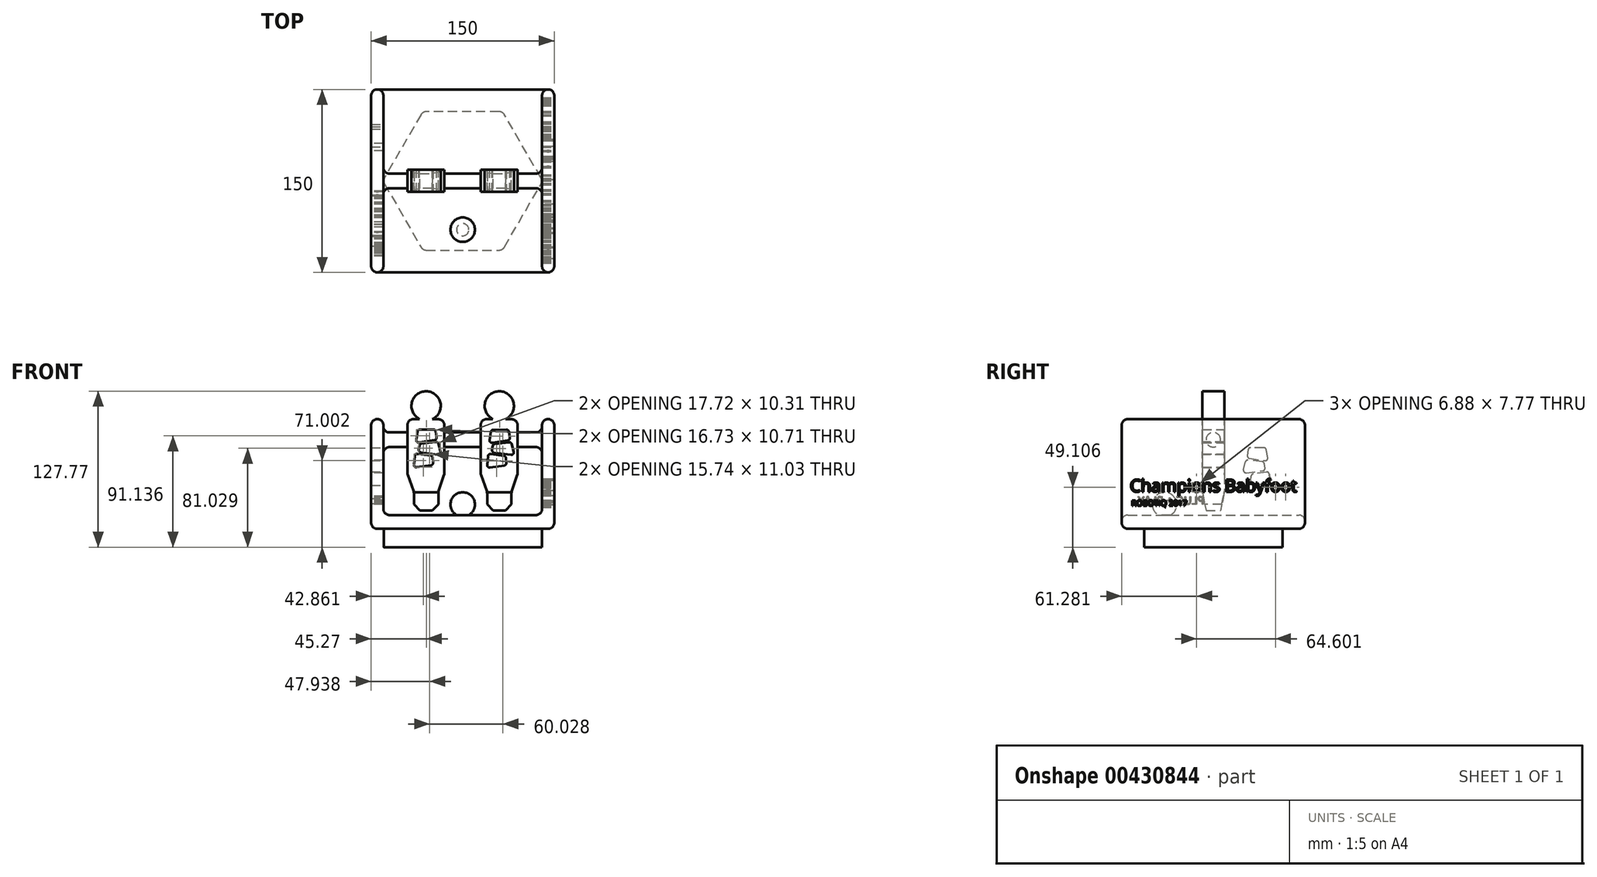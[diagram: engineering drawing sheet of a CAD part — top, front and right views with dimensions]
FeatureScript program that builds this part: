
annotation { "Feature Type Name" : "Feature", "Feature Type Description" : "" }
export const myFeature = defineFeature(function(context is Context, id is Id, definition is map)
    precondition{}
    {
        {
            var Q0;
            Q0=qCreatedBy(makeId("Front.planeOp"),FACE);
            var sketch = newSketch(context, id + "F0", { "sketchPlane" : qUnion([Q0])});
            skLineSegment(sketch, "E0.left", {"start": v(-40, 15) * mm, "end": v(-40, 0) * mm});
            skLineSegment(sketch, "E0.right", {"start": v(-20, 15) * mm, "end": v(-20, 0) * mm});
            skLineSegment(sketch, "E1", {"start": v(-45.3, 75) * mm, "end": v(-35.3, 75) * mm});
            skLineSegment(sketch, "E2", {"start": v(-25, 74.86) * mm, "end": v(-15, 74.86) * mm});
            skArc(sketch, "E3", {"start": v(-25, 74.86) * mm, "mid": v(-29.84, 97.77) * mm, "end": v(-35.3, 75) * mm});
            skLineSegment(sketch, "E4", {"start": v(-40, 0) * mm, "end": v(-30, 0) * mm});
            skLineSegment(sketch, "E5", {"start": v(-30, 0) * mm, "end": v(-20, 0) * mm});
            skLineSegment(sketch, "E6", {"start": v(-15, 74.86) * mm, "end": v(-15, 29.86) * mm});
            skLineSegment(sketch, "E7", {"start": v(-15, 29.86) * mm, "end": v(-20, 15) * mm});
            skLineSegment(sketch, "E8", {"start": v(-45.3, 75) * mm, "end": v(-45.3, 30) * mm});
            skLineSegment(sketch, "E9", {"start": v(-45.3, 30) * mm, "end": v(-40, 15) * mm});
            skLineSegment(sketch, "E10.left", {"start": v(20, 15) * mm, "end": v(20, 0) * mm});
            skLineSegment(sketch, "E10.right", {"start": v(40, 15) * mm, "end": v(40, 0) * mm});
            skLineSegment(sketch, "E11", {"start": v(14.7, 75) * mm, "end": v(24.7, 75) * mm});
            skLineSegment(sketch, "E12", {"start": v(35, 74.86) * mm, "end": v(45, 74.86) * mm});
            skArc(sketch, "E13", {"start": v(35, 74.86) * mm, "mid": v(30.16, 97.77) * mm, "end": v(24.7, 75) * mm});
            skLineSegment(sketch, "E14", {"start": v(20, 0) * mm, "end": v(30, 0) * mm});
            skLineSegment(sketch, "E15", {"start": v(30, 0) * mm, "end": v(40, 0) * mm});
            skLineSegment(sketch, "E16", {"start": v(45, 74.86) * mm, "end": v(45, 29.86) * mm});
            skLineSegment(sketch, "E17", {"start": v(45, 29.86) * mm, "end": v(40, 15) * mm});
            skLineSegment(sketch, "E18", {"start": v(14.7, 75) * mm, "end": v(14.7, 30) * mm});
            skLineSegment(sketch, "E19", {"start": v(14.7, 30) * mm, "end": v(20, 15) * mm});
            skSolve(sketch);
        }
        {
            var Q0;
            Q0 = qSketchRegion(id + "F0", true);
            extrude(context, id + "F1", {"entities" : qUnion([Q0]), "endBound" : BoundingType.SYMMETRIC, "depth" : 18 * mm});
        }
        {
            var Q0;
            Q0=makeQuery(id+"F1.opExtrude","SWEPT_EDGE",EDGE,{"disambiguationData":[OSD([sQuery(id+"F0.wireOp",EDGE,"E1"),sQuery(id+"F0.wireOp",EDGE,"E8")])]});
            var Q1;
            Q1=makeQuery(id+"F1.opExtrude","SWEPT_EDGE",EDGE,{"disambiguationData":[OSD([sQuery(id+"F0.wireOp",EDGE,"E8"),sQuery(id+"F0.wireOp",EDGE,"E9")])]});
            var Q2;
            Q2=makeQuery(id+"F1.opExtrude","SWEPT_EDGE",EDGE,{"disambiguationData":[OSD([sQuery(id+"F0.wireOp",EDGE,"E0.left"),sQuery(id+"F0.wireOp",EDGE,"E9")])]});
            var Q3;
            Q3=makeQuery(id+"F1.opExtrude","SWEPT_EDGE",EDGE,{"disambiguationData":[OSD([sQuery(id+"F0.wireOp",EDGE,"E10.left"),sQuery(id+"F0.wireOp",EDGE,"E19")])]});
            var Q4;
            Q4=makeQuery(id+"F1.opExtrude","SWEPT_EDGE",EDGE,{"disambiguationData":[OSD([sQuery(id+"F0.wireOp",EDGE,"E18"),sQuery(id+"F0.wireOp",EDGE,"E19")])]});
            var Q5;
            Q5=makeQuery(id+"F1.opExtrude","SWEPT_EDGE",EDGE,{"disambiguationData":[OSD([sQuery(id+"F0.wireOp",EDGE,"E11"),sQuery(id+"F0.wireOp",EDGE,"E18")])]});
            var Q6;
            Q6=makeQuery(id+"F1.opExtrude","SWEPT_EDGE",EDGE,{"disambiguationData":[OSD([sQuery(id+"F0.wireOp",EDGE,"E2"),sQuery(id+"F0.wireOp",EDGE,"E6")])]});
            var Q7;
            Q7=makeQuery(id+"F1.opExtrude","SWEPT_EDGE",EDGE,{"disambiguationData":[OSD([sQuery(id+"F0.wireOp",EDGE,"E6"),sQuery(id+"F0.wireOp",EDGE,"E7")])]});
            var Q8;
            Q8=makeQuery(id+"F1.opExtrude","SWEPT_EDGE",EDGE,{"disambiguationData":[OSD([sQuery(id+"F0.wireOp",EDGE,"E0.right"),sQuery(id+"F0.wireOp",EDGE,"E7")])]});
            var Q9;
            Q9=makeQuery(id+"F1.opExtrude","SWEPT_EDGE",EDGE,{"disambiguationData":[OSD([sQuery(id+"F0.wireOp",EDGE,"E10.right"),sQuery(id+"F0.wireOp",EDGE,"E17")])]});
            var Q10;
            Q10=makeQuery(id+"F1.opExtrude","SWEPT_EDGE",EDGE,{"disambiguationData":[OSD([sQuery(id+"F0.wireOp",EDGE,"E16"),sQuery(id+"F0.wireOp",EDGE,"E17")])]});
            var Q11;
            Q11=makeQuery(id+"F1.opExtrude","SWEPT_EDGE",EDGE,{"disambiguationData":[OSD([sQuery(id+"F0.wireOp",EDGE,"E12"),sQuery(id+"F0.wireOp",EDGE,"E16")])]});
            fillet(context, id + "F2", {"entities" : qUnion([Q0, Q1, Q2, Q3, Q4, Q5, Q6, Q7, Q8, Q9, Q10, Q11]), "radius" : 5 * mm, "tangentPropagation" : true, "allowEdgeOverflow" : false});
        }
        {
            var Q0;
            Q0=makeQuery(id+"F1.opExtrude","SWEPT_EDGE",EDGE,{"disambiguationData":[OSD([sQuery(id+"F0.wireOp",EDGE,"E0.left"),sQuery(id+"F0.wireOp",EDGE,"E4")])]});
            var Q1;
            Q1=makeQuery(id+"F1.opExtrude","SWEPT_EDGE",EDGE,{"disambiguationData":[OSD([sQuery(id+"F0.wireOp",EDGE,"E0.right"),sQuery(id+"F0.wireOp",EDGE,"E5")])]});
            var Q2;
            Q2=makeQuery(id+"F1.opExtrude","SWEPT_EDGE",EDGE,{"disambiguationData":[OSD([sQuery(id+"F0.wireOp",EDGE,"E10.right"),sQuery(id+"F0.wireOp",EDGE,"E15")])]});
            var Q3;
            Q3=makeQuery(id+"F1.opExtrude","SWEPT_EDGE",EDGE,{"disambiguationData":[OSD([sQuery(id+"F0.wireOp",EDGE,"E10.left"),sQuery(id+"F0.wireOp",EDGE,"E14")])]});
            chamfer(context, id + "F3", {"entities" : qUnion([Q0, Q1, Q2, Q3]), "width" : 5 * mm, "tangentPropagation" : true});
        }
        {
            var Q0;
            Q0=makeQuery(id+"F1.opExtrude","CAP_EDGE",EDGE,{"disambiguationData":[OSD([sQuery(id+"F0.wireOp",EDGE,"E4"),sQuery(id+"F0.wireOp",EDGE,"E5")])],"isStart":false});
            var Q1;
            Q1=makeQuery(id+"F1.opExtrude","CAP_EDGE",EDGE,{"disambiguationData":[OSD([sQuery(id+"F0.wireOp",EDGE,"E14"),sQuery(id+"F0.wireOp",EDGE,"E15")])],"isStart":false});
            var Q2;
            Q2=makeQuery(id+"F1.opExtrude","CAP_EDGE",EDGE,{"disambiguationData":[OSD([sQuery(id+"F0.wireOp",EDGE,"E14"),sQuery(id+"F0.wireOp",EDGE,"E15")])],"isStart":true});
            var Q3;
            Q3=makeQuery(id+"F1.opExtrude","CAP_EDGE",EDGE,{"disambiguationData":[OSD([sQuery(id+"F0.wireOp",EDGE,"E4"),sQuery(id+"F0.wireOp",EDGE,"E5")])],"isStart":true});
            chamfer(context, id + "F4", {"entities" : qUnion([Q0, Q1, Q2, Q3]), "chamferType" : ChamferType.TWO_OFFSETS, "width1" : 15 * mm, "oppositeDirection" : false, "width2" : 3 * mm, "tangentPropagation" : true});
        }
        {
            var Q0;
            Q0=qCreatedBy(makeId("Right.planeOp"),FACE);
            var sketch = newSketch(context, id + "F5", { "sketchPlane" : qUnion([Q0])});
            skCircle(sketch, "E20", {"center": v(0, 58) * mm, "radius": 6 * mm});
            skSolve(sketch);
        }
        {
            var Q0;
            Q0 = qSketchRegion(id + "F5", true);
            extrude(context, id + "F6", {"entities" : qUnion([Q0]), "operationType" : NewBodyOperationType.ADD, "endBound" : BoundingType.SYMMETRIC, "depth" : 150 * mm});
        }
        {
            var Q0;
            Q0=qCreatedBy(makeId("Front.planeOp"),FACE);
            cPlane(context, id + "F7", {"entities" : qUnion([Q0]), "cplaneType" : CPlaneType.OFFSET, "offset" : 40 * mm, "width" : 150 * mm, "height" : 150 * mm});
        }
        {
            var Q0;
            Q0=qCreatedBy(id+"F7.planeOp",FACE);
            var sketch = newSketch(context, id + "F8", { "sketchPlane" : qUnion([Q0])});
            skPoint(sketch, "E21", {"position": v(0, 4.98) * mm});
            skLineSegment(sketch, "E22", {"start": v(-10, 4.93) * mm, "end": v(10, 4.93) * mm});
            skArc(sketch, "E23", {"start": v(10, 4.93) * mm, "mid": v(0, 14.93) * mm, "end": v(-10, 4.93) * mm});
            skSolve(sketch);
        }
        {
            var Q0;
            Q0=qCreatedBy(makeId("Front.planeOp"),FACE);
            var sketch = newSketch(context, id + "F9", { "sketchPlane" : qUnion([Q0])});
            skLineSegment(sketch, "E24.top", {"start": v(-75, -15) * mm, "end": v(75, -15) * mm});
            skLineSegment(sketch, "E25", {"start": v(75, -15) * mm, "end": v(75, 75) * mm});
            skLineSegment(sketch, "E26", {"start": v(75, 75) * mm, "end": v(65, 75) * mm});
            skLineSegment(sketch, "E27", {"start": v(65, 75) * mm, "end": v(65, 0) * mm});
            skLineSegment(sketch, "E28", {"start": v(-65, 1.11) * mm, "end": v(-65, 75) * mm});
            skLineSegment(sketch, "E29", {"start": v(-75, -15) * mm, "end": v(-75, 75) * mm});
            skLineSegment(sketch, "E30", {"start": v(-75, 75) * mm, "end": v(-65, 75) * mm});
            skLineSegment(sketch, "E31", {"start": v(65, 0) * mm, "end": v(65, -3.72) * mm});
            skLineSegment(sketch, "E32", {"start": v(65, -3.72) * mm, "end": v(-65, -3.72) * mm});
            skLineSegment(sketch, "E33", {"start": v(-65, 1.11) * mm, "end": v(-65, -3.72) * mm});
            skSolve(sketch);
        }
        {
            var Q0;
            Q0 = qSketchRegion(id + "F9", true);
            extrude(context, id + "F10", {"entities" : qUnion([Q0]), "operationType" : NewBodyOperationType.ADD, "endBound" : BoundingType.SYMMETRIC, "depth" : 150 * mm});
        }
        {
            var Q0;
            Q0=makeQuery(id+"F10.opExtrude","SWEPT_EDGE",EDGE,{"disambiguationData":[OSD([sQuery(id+"F9.wireOp",EDGE,"E29"),sQuery(id+"F9.wireOp",EDGE,"E30")])]});
            var Q1;
            Q1=makeQuery(id+"F10.opExtrude","CAP_EDGE",EDGE,{"disambiguationData":[OSD([sQuery(id+"F9.wireOp",EDGE,"E30")])],"isStart":false});
            var Q2;
            Q2=makeQuery(id+"F10.opExtrude","CAP_EDGE",EDGE,{"disambiguationData":[OSD([sQuery(id+"F9.wireOp",EDGE,"E30")])],"isStart":true});
            var Q3;
            Q3=makeQuery(id+"F10.opExtrude","SWEPT_EDGE",EDGE,{"disambiguationData":[OSD([sQuery(id+"F9.wireOp",EDGE,"E28"),sQuery(id+"F9.wireOp",EDGE,"E30")])]});
            var Q4;
            Q4=makeQuery(id+"F10.opExtrude","CAP_EDGE",EDGE,{"disambiguationData":[OSD([sQuery(id+"F9.wireOp",EDGE,"E28"),sQuery(id+"F9.wireOp",EDGE,"E33")])],"isStart":true});
            var Q5;
            Q5=makeQuery(id+"F10.opExtrude","CAP_EDGE",EDGE,{"disambiguationData":[OSD([sQuery(id+"F9.wireOp",EDGE,"E29")])],"isStart":true});
            var Q6;
            Q6=makeQuery(id+"F10.opExtrude","CAP_EDGE",EDGE,{"disambiguationData":[OSD([sQuery(id+"F9.wireOp",EDGE,"E29")])],"isStart":false});
            var Q7;
            Q7=makeQuery(id+"F10.opExtrude","CAP_EDGE",EDGE,{"disambiguationData":[OSD([sQuery(id+"F9.wireOp",EDGE,"E28"),sQuery(id+"F9.wireOp",EDGE,"E33")])],"isStart":false});
            var Q8;
            Q8=makeQuery(id+"F10.opExtrude","CAP_EDGE",EDGE,{"disambiguationData":[OSD([sQuery(id+"F9.wireOp",EDGE,"E32")])],"isStart":false});
            var Q9;
            Q9=makeQuery(id+"F10.opExtrude","CAP_EDGE",EDGE,{"disambiguationData":[OSD([sQuery(id+"F9.wireOp",EDGE,"E24.top")])],"isStart":false});
            var Q10;
            Q10=makeQuery(id+"F10.opExtrude","SWEPT_EDGE",EDGE,{"disambiguationData":[OSD([sQuery(id+"F9.wireOp",EDGE,"E24.top"),sQuery(id+"F9.wireOp",EDGE,"E29")])]});
            var Q11;
            Q11=makeQuery(id+"F10.opExtrude","CAP_EDGE",EDGE,{"disambiguationData":[OSD([sQuery(id+"F9.wireOp",EDGE,"E24.top")])],"isStart":true});
            var Q12;
            Q12=makeQuery(id+"F10.opExtrude","SWEPT_EDGE",EDGE,{"disambiguationData":[OSD([sQuery(id+"F9.wireOp",EDGE,"E24.top"),sQuery(id+"F9.wireOp",EDGE,"E25")])]});
            var Q13;
            Q13=makeQuery(id+"F10.opExtrude","CAP_EDGE",EDGE,{"disambiguationData":[OSD([sQuery(id+"F9.wireOp",EDGE,"E25")])],"isStart":false});
            var Q14;
            Q14=makeQuery(id+"F10.opExtrude","CAP_EDGE",EDGE,{"disambiguationData":[OSD([sQuery(id+"F9.wireOp",EDGE,"E27"),sQuery(id+"F9.wireOp",EDGE,"E31")])],"isStart":false});
            var Q15;
            Q15=makeQuery(id+"F10.opExtrude","CAP_EDGE",EDGE,{"disambiguationData":[OSD([sQuery(id+"F9.wireOp",EDGE,"E25")])],"isStart":true});
            var Q16;
            Q16=makeQuery(id+"F10.opExtrude","CAP_EDGE",EDGE,{"disambiguationData":[OSD([sQuery(id+"F9.wireOp",EDGE,"E27"),sQuery(id+"F9.wireOp",EDGE,"E31")])],"isStart":true});
            var Q17;
            Q17=makeQuery(id+"F10.opExtrude","CAP_EDGE",EDGE,{"disambiguationData":[OSD([sQuery(id+"F9.wireOp",EDGE,"E32")])],"isStart":true});
            var Q18;
            Q18=makeQuery(id+"F10.opExtrude","CAP_EDGE",EDGE,{"disambiguationData":[OSD([sQuery(id+"F9.wireOp",EDGE,"E26")])],"isStart":true});
            var Q19;
            Q19=makeQuery(id+"F10.opExtrude","SWEPT_EDGE",EDGE,{"disambiguationData":[OSD([sQuery(id+"F9.wireOp",EDGE,"E25"),sQuery(id+"F9.wireOp",EDGE,"E26")])]});
            var Q20;
            Q20=makeQuery(id+"F10.opExtrude","SWEPT_EDGE",EDGE,{"disambiguationData":[OSD([sQuery(id+"F9.wireOp",EDGE,"E26"),sQuery(id+"F9.wireOp",EDGE,"E27")])]});
            var Q21;
            Q21=makeQuery(id+"F10.opExtrude","SWEPT_EDGE",EDGE,{"disambiguationData":[OSD([sQuery(id+"F9.wireOp",EDGE,"E32"),sQuery(id+"F9.wireOp",EDGE,"E33")])]});
            var Q22;
            Q22=makeQuery(id+"F10.opExtrude","SWEPT_FACE",FACE,{"disambiguationData":[OSD([sQuery(id+"F9.wireOp",EDGE,"E27"),sQuery(id+"F9.wireOp",EDGE,"E31")])]});
            var Q23;
            Q23=makeQuery(id+"F10.opExtrude","CAP_EDGE",EDGE,{"disambiguationData":[OSD([sQuery(id+"F9.wireOp",EDGE,"E26")])],"isStart":false});
            var Q24;
            {var subQ0=sQuery(id+"F5.wireOp",EDGE,"E20");Q24=makeQuery(id+"F10.boolean.opBoolean","INTERSECT",EDGE,{"derivedFrom":[makeQuery(id+"F6.boolean.opBoolean","SPLIT",FACE,{"disambiguationData":[TD([makeQuery(id+"F1.opExtrude","SWEPT_FACE",FACE,{"disambiguationData":[OSD([sQuery(id+"F0.wireOp",EDGE,"E8")])]})])],"derivedFrom":makeQuery(id+"F6.opExtrude","SWEPT_FACE",FACE,{"disambiguationData":[OSD([subQ0])]})}),makeQuery(id+"F10.opExtrude","SWEPT_FACE",FACE,{"disambiguationData":[OSD([sQuery(id+"F9.wireOp",EDGE,"E28"),sQuery(id+"F9.wireOp",EDGE,"E33")])]})]});}
            fillet(context, id + "F11", {"entities" : qUnion([Q0, Q1, Q2, Q3, Q4, Q5, Q6, Q7, Q8, Q9, Q10, Q11, Q12, Q13, Q14, Q15, Q16, Q17, Q18, Q19, Q20, Q21, Q22, Q23, Q24]), "radius" : 5 * mm, "tangentPropagation" : true, "allowEdgeOverflow" : false});
        }
        {
            var Q0;
            Q0=makeQuery(id+"F10.boolean.opBoolean","MERGE",FACE,{"derivedFrom":[makeQuery(id+"F6.opExtrude","CAP_FACE",FACE,{"disambiguationData":[OSD([sQuery(id+"F5.wireOp",EDGE,"E20")])],"isStart":false}),makeQuery(id+"F10.opExtrude","SWEPT_FACE",FACE,{"disambiguationData":[OSD([sQuery(id+"F9.wireOp",EDGE,"E25")])]})]});
            var sketch = newSketch(context, id + "F12", { "sketchPlane" : qUnion([Q0])});
            skText(sketch, "E34", { "text": "Champions Babyfoot", "fontName": "OpenSans-Regular.ttf"});
            skText(sketch, "E35", { "text": "ROBOTIQ 2017", "fontName": "OpenSans-Regular.ttf"});
            const initialGuessF12  = {"E34": [-0.0683, 0.01536, 1, 0, 0.01008], "E35": [-0.06708, 0.00377, 1, 0, 0.0047]};
            skSetInitialGuess(sketch, initialGuessF12);
            skSolve(sketch);
        }
        {
            var Q0;
            Q0 = qSketchRegion(id + "F12", true);
            extrude(context, id + "F13", {"entities" : qUnion([Q0]), "operationType" : NewBodyOperationType.REMOVE, "oppositeDirection" : true, "depth" : 25 * mm});
        }
        {
            var Q0;
            Q0=makeQuery(id+"F10.boolean.opBoolean","MERGE",FACE,{"derivedFrom":[makeQuery(id+"F6.opExtrude","CAP_FACE",FACE,{"disambiguationData":[OSD([sQuery(id+"F5.wireOp",EDGE,"E20")])],"isStart":true}),makeQuery(id+"F10.opExtrude","SWEPT_FACE",FACE,{"disambiguationData":[OSD([sQuery(id+"F9.wireOp",EDGE,"E29")])]})]});
            var sketch = newSketch(context, id + "F14", { "sketchPlane" : qUnion([Q0])});
            skLineSegment(sketch, "E36", {"start": v(-43.16, 51.43) * mm, "end": v(-44.96, 40.45) * mm});
            skLineSegment(sketch, "E37", {"start": v(-44.96, 40.45) * mm, "end": v(-27.5, 43.23) * mm});
            skLineSegment(sketch, "E38", {"start": v(-27.5, 43.23) * mm, "end": v(-28.84, 51.6) * mm});
            skLineSegment(sketch, "E39", {"start": v(-28.84, 51.6) * mm, "end": v(-43.16, 51.43) * mm});
            skLineSegment(sketch, "E40", {"start": v(-41.54, 39.83) * mm, "end": v(-42.66, 32.89) * mm});
            skLineSegment(sketch, "E41", {"start": v(-42.66, 32.89) * mm, "end": v(-24, 30.61) * mm});
            skLineSegment(sketch, "E42", {"start": v(-26.68, 41.46) * mm, "end": v(-41.54, 39.83) * mm});
            skLineSegment(sketch, "E43", {"start": v(-26.68, 41.46) * mm, "end": v(-24, 30.61) * mm});
            skLineSegment(sketch, "E44", {"start": v(-45.62, 31.87) * mm, "end": v(-46.67, 20.24) * mm});
            skLineSegment(sketch, "E45", {"start": v(-46.67, 20.24) * mm, "end": v(-30.53, 22.48) * mm});
            skLineSegment(sketch, "E46", {"start": v(-31.2, 29.92) * mm, "end": v(-45.62, 31.87) * mm});
            skLineSegment(sketch, "E47", {"start": v(-31.2, 29.92) * mm, "end": v(-30.53, 22.48) * mm});
            skSolve(sketch);
        }
        {
            var Q0;
            Q0=makeQuery(id+"F14.imprint","IMPRINT",FACE,{"disambiguationData":[TD([[makeQuery(id+"F14.imprint","IMPRINT",EDGE,{"derivedFrom":sQuery(id+"F14.wireOp",EDGE,"E36")}),1.0]])]});
            var Q1;
            Q1=makeQuery(id+"F14.imprint","IMPRINT",FACE,{"disambiguationData":[TD([[makeQuery(id+"F14.imprint","IMPRINT",EDGE,{"derivedFrom":sQuery(id+"F14.wireOp",EDGE,"E40")}),1.0]])]});
            var Q2;
            Q2=makeQuery(id+"F14.imprint","IMPRINT",FACE,{"disambiguationData":[TD([[makeQuery(id+"F14.imprint","IMPRINT",EDGE,{"derivedFrom":sQuery(id+"F14.wireOp",EDGE,"E44")}),1.0]])]});
            extrude(context, id + "F15", {"entities" : qUnion([Q0, Q1, Q2]), "operationType" : NewBodyOperationType.REMOVE, "oppositeDirection" : true, "depth" : 25 * mm});
        }
        {
            var Q0;
            Q0=makeQuery(id+"F15.boolean.opBoolean","COPY",EDGE,{"derivedFrom":makeQuery(id+"F15.opExtrude","SWEPT_EDGE",EDGE,{"disambiguationData":[OSD([sQuery(id+"F14.wireOp",EDGE,"E41"),sQuery(id+"F14.wireOp",EDGE,"E43")])]})});
            var Q1;
            Q1=makeQuery(id+"F15.boolean.opBoolean","COPY",EDGE,{"derivedFrom":makeQuery(id+"F15.opExtrude","SWEPT_EDGE",EDGE,{"disambiguationData":[OSD([sQuery(id+"F14.wireOp",EDGE,"E42"),sQuery(id+"F14.wireOp",EDGE,"E43")])]})});
            var Q2;
            Q2=makeQuery(id+"F15.boolean.opBoolean","COPY",EDGE,{"derivedFrom":makeQuery(id+"F15.opExtrude","SWEPT_EDGE",EDGE,{"disambiguationData":[OSD([sQuery(id+"F14.wireOp",EDGE,"E40"),sQuery(id+"F14.wireOp",EDGE,"E41")])]})});
            var Q3;
            Q3=makeQuery(id+"F15.boolean.opBoolean","COPY",EDGE,{"derivedFrom":makeQuery(id+"F15.opExtrude","SWEPT_EDGE",EDGE,{"disambiguationData":[OSD([sQuery(id+"F14.wireOp",EDGE,"E40"),sQuery(id+"F14.wireOp",EDGE,"E42")])]})});
            var Q4;
            Q4=makeQuery(id+"F15.boolean.opBoolean","COPY",EDGE,{"derivedFrom":makeQuery(id+"F15.opExtrude","SWEPT_EDGE",EDGE,{"disambiguationData":[OSD([sQuery(id+"F14.wireOp",EDGE,"E44"),sQuery(id+"F14.wireOp",EDGE,"E46")])]})});
            var Q5;
            Q5=makeQuery(id+"F15.boolean.opBoolean","COPY",EDGE,{"derivedFrom":makeQuery(id+"F15.opExtrude","SWEPT_EDGE",EDGE,{"disambiguationData":[OSD([sQuery(id+"F14.wireOp",EDGE,"E46"),sQuery(id+"F14.wireOp",EDGE,"E47")])]})});
            var Q6;
            Q6=makeQuery(id+"F15.boolean.opBoolean","COPY",EDGE,{"derivedFrom":makeQuery(id+"F15.opExtrude","SWEPT_EDGE",EDGE,{"disambiguationData":[OSD([sQuery(id+"F14.wireOp",EDGE,"E45"),sQuery(id+"F14.wireOp",EDGE,"E47")])]})});
            var Q7;
            Q7=makeQuery(id+"F15.boolean.opBoolean","COPY",EDGE,{"derivedFrom":makeQuery(id+"F15.opExtrude","SWEPT_EDGE",EDGE,{"disambiguationData":[OSD([sQuery(id+"F14.wireOp",EDGE,"E44"),sQuery(id+"F14.wireOp",EDGE,"E45")])]})});
            var Q8;
            Q8=makeQuery(id+"F15.boolean.opBoolean","COPY",EDGE,{"derivedFrom":makeQuery(id+"F15.opExtrude","SWEPT_EDGE",EDGE,{"disambiguationData":[OSD([sQuery(id+"F14.wireOp",EDGE,"E37"),sQuery(id+"F14.wireOp",EDGE,"E38")])]})});
            var Q9;
            Q9=makeQuery(id+"F15.boolean.opBoolean","COPY",EDGE,{"derivedFrom":makeQuery(id+"F15.opExtrude","SWEPT_EDGE",EDGE,{"disambiguationData":[OSD([sQuery(id+"F14.wireOp",EDGE,"E38"),sQuery(id+"F14.wireOp",EDGE,"E39")])]})});
            var Q10;
            Q10=makeQuery(id+"F15.boolean.opBoolean","COPY",EDGE,{"derivedFrom":makeQuery(id+"F15.opExtrude","SWEPT_EDGE",EDGE,{"disambiguationData":[OSD([sQuery(id+"F14.wireOp",EDGE,"E36"),sQuery(id+"F14.wireOp",EDGE,"E37")])]})});
            var Q11;
            Q11=makeQuery(id+"F15.boolean.opBoolean","COPY",EDGE,{"derivedFrom":makeQuery(id+"F15.opExtrude","SWEPT_EDGE",EDGE,{"disambiguationData":[OSD([sQuery(id+"F14.wireOp",EDGE,"E36"),sQuery(id+"F14.wireOp",EDGE,"E39")])]})});
            fillet(context, id + "F16", {"entities" : qUnion([Q0, Q1, Q2, Q3, Q4, Q5, Q6, Q7, Q8, Q9, Q10, Q11]), "radius" : 2 * mm, "tangentPropagation" : true, "allowEdgeOverflow" : false});
        }
        {
            var Q0;
            Q0=makeQuery(id+"F1.opExtrude","CAP_FACE",FACE,{"disambiguationData":[OSD([sQuery(id+"F0.wireOp",EDGE,"E0.left"),sQuery(id+"F0.wireOp",EDGE,"E0.right"),sQuery(id+"F0.wireOp",EDGE,"E1"),sQuery(id+"F0.wireOp",EDGE,"E2"),sQuery(id+"F0.wireOp",EDGE,"E3"),sQuery(id+"F0.wireOp",EDGE,"E4"),sQuery(id+"F0.wireOp",EDGE,"E5"),sQuery(id+"F0.wireOp",EDGE,"E6"),sQuery(id+"F0.wireOp",EDGE,"E7"),sQuery(id+"F0.wireOp",EDGE,"E8"),sQuery(id+"F0.wireOp",EDGE,"E9")])],"isStart":false});
            var sketch = newSketch(context, id + "F17", { "sketchPlane" : qUnion([Q0])});
            skLineSegment(sketch, "E48", {"start": v(-36.73, 66.34) * mm, "end": v(-38.52, 55.37) * mm});
            skLineSegment(sketch, "E49", {"start": v(-38.52, 55.37) * mm, "end": v(-21.07, 58.15) * mm});
            skLineSegment(sketch, "E50", {"start": v(-21.07, 58.15) * mm, "end": v(-22.4, 66.51) * mm});
            skLineSegment(sketch, "E51", {"start": v(-22.4, 66.51) * mm, "end": v(-36.73, 66.34) * mm});
            skLineSegment(sketch, "E52", {"start": v(-35.11, 54.74) * mm, "end": v(-36.23, 47.8) * mm});
            skLineSegment(sketch, "E53", {"start": v(-36.23, 47.8) * mm, "end": v(-17.56, 45.52) * mm});
            skLineSegment(sketch, "E54", {"start": v(-20.25, 56.37) * mm, "end": v(-35.11, 54.74) * mm});
            skLineSegment(sketch, "E55", {"start": v(-20.25, 56.37) * mm, "end": v(-17.56, 45.52) * mm});
            skLineSegment(sketch, "E56", {"start": v(-39.18, 46.78) * mm, "end": v(-40.24, 35.15) * mm});
            skLineSegment(sketch, "E57", {"start": v(-40.24, 35.15) * mm, "end": v(-24.1, 37.4) * mm});
            skLineSegment(sketch, "E58", {"start": v(-24.78, 44.83) * mm, "end": v(-39.18, 46.78) * mm});
            skLineSegment(sketch, "E59", {"start": v(-24.78, 44.83) * mm, "end": v(-24.1, 37.4) * mm});
            skLineSegment(sketch, "E60", {"start": v(23.3, 66.12) * mm, "end": v(21.5, 55.15) * mm});
            skLineSegment(sketch, "E61", {"start": v(21.5, 55.15) * mm, "end": v(38.96, 57.93) * mm});
            skLineSegment(sketch, "E62", {"start": v(38.96, 57.93) * mm, "end": v(37.62, 66.3) * mm});
            skLineSegment(sketch, "E63", {"start": v(37.62, 66.3) * mm, "end": v(23.3, 66.12) * mm});
            skLineSegment(sketch, "E64", {"start": v(24.92, 54.52) * mm, "end": v(23.8, 47.58) * mm});
            skLineSegment(sketch, "E65", {"start": v(23.8, 47.58) * mm, "end": v(42.47, 45.3) * mm});
            skLineSegment(sketch, "E66", {"start": v(39.78, 56.15) * mm, "end": v(24.92, 54.52) * mm});
            skLineSegment(sketch, "E67", {"start": v(39.78, 56.15) * mm, "end": v(42.47, 45.3) * mm});
            skLineSegment(sketch, "E68", {"start": v(20.84, 46.56) * mm, "end": v(19.8, 34.93) * mm});
            skLineSegment(sketch, "E69", {"start": v(19.8, 34.93) * mm, "end": v(35.93, 37.17) * mm});
            skLineSegment(sketch, "E70", {"start": v(35.25, 44.6) * mm, "end": v(20.84, 46.56) * mm});
            skLineSegment(sketch, "E71", {"start": v(35.25, 44.6) * mm, "end": v(35.93, 37.17) * mm});
            skSolve(sketch);
        }
        {
            var Q0;
            Q0 = qSketchRegion(id + "F17", true);
            extrude(context, id + "F18", {"entities" : qUnion([Q0]), "operationType" : NewBodyOperationType.REMOVE, "oppositeDirection" : true, "depth" : 25 * mm});
        }
        {
            var Q0;
            Q0=makeQuery(id+"F18.boolean.opBoolean","COPY",EDGE,{"derivedFrom":makeQuery(id+"F18.opExtrude","SWEPT_EDGE",EDGE,{"disambiguationData":[OSD([sQuery(id+"F17.wireOp",EDGE,"E48"),sQuery(id+"F17.wireOp",EDGE,"E51")])]})});
            var Q1;
            Q1=makeQuery(id+"F18.boolean.opBoolean","COPY",EDGE,{"derivedFrom":makeQuery(id+"F18.opExtrude","SWEPT_EDGE",EDGE,{"disambiguationData":[OSD([sQuery(id+"F17.wireOp",EDGE,"E52"),sQuery(id+"F17.wireOp",EDGE,"E54")])]})});
            var Q2;
            Q2=makeQuery(id+"F18.boolean.opBoolean","COPY",EDGE,{"derivedFrom":makeQuery(id+"F18.opExtrude","SWEPT_EDGE",EDGE,{"disambiguationData":[OSD([sQuery(id+"F17.wireOp",EDGE,"E56"),sQuery(id+"F17.wireOp",EDGE,"E58")])]})});
            var Q3;
            Q3=makeQuery(id+"F18.boolean.opBoolean","COPY",EDGE,{"derivedFrom":makeQuery(id+"F18.opExtrude","SWEPT_EDGE",EDGE,{"disambiguationData":[OSD([sQuery(id+"F17.wireOp",EDGE,"E50"),sQuery(id+"F17.wireOp",EDGE,"E51")])]})});
            var Q4;
            Q4=makeQuery(id+"F18.boolean.opBoolean","COPY",EDGE,{"derivedFrom":makeQuery(id+"F18.opExtrude","SWEPT_EDGE",EDGE,{"disambiguationData":[OSD([sQuery(id+"F17.wireOp",EDGE,"E54"),sQuery(id+"F17.wireOp",EDGE,"E55")])]})});
            var Q5;
            Q5=makeQuery(id+"F18.boolean.opBoolean","COPY",EDGE,{"derivedFrom":makeQuery(id+"F18.opExtrude","SWEPT_EDGE",EDGE,{"disambiguationData":[OSD([sQuery(id+"F17.wireOp",EDGE,"E58"),sQuery(id+"F17.wireOp",EDGE,"E59")])]})});
            var Q6;
            Q6=makeQuery(id+"F18.boolean.opBoolean","COPY",EDGE,{"derivedFrom":makeQuery(id+"F18.opExtrude","SWEPT_EDGE",EDGE,{"disambiguationData":[OSD([sQuery(id+"F17.wireOp",EDGE,"E70"),sQuery(id+"F17.wireOp",EDGE,"E71")])]})});
            var Q7;
            Q7=makeQuery(id+"F18.boolean.opBoolean","COPY",EDGE,{"derivedFrom":makeQuery(id+"F18.opExtrude","SWEPT_EDGE",EDGE,{"disambiguationData":[OSD([sQuery(id+"F17.wireOp",EDGE,"E66"),sQuery(id+"F17.wireOp",EDGE,"E67")])]})});
            var Q8;
            Q8=makeQuery(id+"F18.boolean.opBoolean","COPY",EDGE,{"derivedFrom":makeQuery(id+"F18.opExtrude","SWEPT_EDGE",EDGE,{"disambiguationData":[OSD([sQuery(id+"F17.wireOp",EDGE,"E62"),sQuery(id+"F17.wireOp",EDGE,"E63")])]})});
            var Q9;
            Q9=makeQuery(id+"F18.boolean.opBoolean","COPY",EDGE,{"derivedFrom":makeQuery(id+"F18.opExtrude","SWEPT_EDGE",EDGE,{"disambiguationData":[OSD([sQuery(id+"F17.wireOp",EDGE,"E68"),sQuery(id+"F17.wireOp",EDGE,"E70")])]})});
            var Q10;
            Q10=makeQuery(id+"F18.boolean.opBoolean","COPY",EDGE,{"derivedFrom":makeQuery(id+"F18.opExtrude","SWEPT_EDGE",EDGE,{"disambiguationData":[OSD([sQuery(id+"F17.wireOp",EDGE,"E64"),sQuery(id+"F17.wireOp",EDGE,"E66")])]})});
            var Q11;
            Q11=makeQuery(id+"F18.boolean.opBoolean","COPY",EDGE,{"derivedFrom":makeQuery(id+"F18.opExtrude","SWEPT_EDGE",EDGE,{"disambiguationData":[OSD([sQuery(id+"F17.wireOp",EDGE,"E60"),sQuery(id+"F17.wireOp",EDGE,"E63")])]})});
            var Q12;
            Q12=makeQuery(id+"F18.boolean.opBoolean","COPY",EDGE,{"derivedFrom":makeQuery(id+"F18.opExtrude","SWEPT_EDGE",EDGE,{"disambiguationData":[OSD([sQuery(id+"F17.wireOp",EDGE,"E68"),sQuery(id+"F17.wireOp",EDGE,"E69")])]})});
            var Q13;
            Q13=makeQuery(id+"F18.boolean.opBoolean","COPY",EDGE,{"derivedFrom":makeQuery(id+"F18.opExtrude","SWEPT_EDGE",EDGE,{"disambiguationData":[OSD([sQuery(id+"F17.wireOp",EDGE,"E64"),sQuery(id+"F17.wireOp",EDGE,"E65")])]})});
            var Q14;
            Q14=makeQuery(id+"F18.boolean.opBoolean","COPY",EDGE,{"derivedFrom":makeQuery(id+"F18.opExtrude","SWEPT_EDGE",EDGE,{"disambiguationData":[OSD([sQuery(id+"F17.wireOp",EDGE,"E60"),sQuery(id+"F17.wireOp",EDGE,"E61")])]})});
            var Q15;
            Q15=makeQuery(id+"F18.boolean.opBoolean","COPY",EDGE,{"derivedFrom":makeQuery(id+"F18.opExtrude","SWEPT_EDGE",EDGE,{"disambiguationData":[OSD([sQuery(id+"F17.wireOp",EDGE,"E52"),sQuery(id+"F17.wireOp",EDGE,"E53")])]})});
            var Q16;
            Q16=makeQuery(id+"F18.boolean.opBoolean","COPY",EDGE,{"derivedFrom":makeQuery(id+"F18.opExtrude","SWEPT_EDGE",EDGE,{"disambiguationData":[OSD([sQuery(id+"F17.wireOp",EDGE,"E56"),sQuery(id+"F17.wireOp",EDGE,"E57")])]})});
            var Q17;
            Q17=makeQuery(id+"F18.boolean.opBoolean","COPY",EDGE,{"derivedFrom":makeQuery(id+"F18.opExtrude","SWEPT_EDGE",EDGE,{"disambiguationData":[OSD([sQuery(id+"F17.wireOp",EDGE,"E48"),sQuery(id+"F17.wireOp",EDGE,"E49")])]})});
            var Q18;
            Q18=makeQuery(id+"F18.boolean.opBoolean","COPY",EDGE,{"derivedFrom":makeQuery(id+"F18.opExtrude","SWEPT_EDGE",EDGE,{"disambiguationData":[OSD([sQuery(id+"F17.wireOp",EDGE,"E49"),sQuery(id+"F17.wireOp",EDGE,"E50")])]})});
            var Q19;
            Q19=makeQuery(id+"F18.boolean.opBoolean","COPY",EDGE,{"derivedFrom":makeQuery(id+"F18.opExtrude","SWEPT_EDGE",EDGE,{"disambiguationData":[OSD([sQuery(id+"F17.wireOp",EDGE,"E53"),sQuery(id+"F17.wireOp",EDGE,"E55")])]})});
            var Q20;
            Q20=makeQuery(id+"F18.boolean.opBoolean","COPY",EDGE,{"derivedFrom":makeQuery(id+"F18.opExtrude","SWEPT_EDGE",EDGE,{"disambiguationData":[OSD([sQuery(id+"F17.wireOp",EDGE,"E57"),sQuery(id+"F17.wireOp",EDGE,"E59")])]})});
            var Q21;
            Q21=makeQuery(id+"F18.boolean.opBoolean","COPY",EDGE,{"derivedFrom":makeQuery(id+"F18.opExtrude","SWEPT_EDGE",EDGE,{"disambiguationData":[OSD([sQuery(id+"F17.wireOp",EDGE,"E69"),sQuery(id+"F17.wireOp",EDGE,"E71")])]})});
            var Q22;
            Q22=makeQuery(id+"F18.boolean.opBoolean","COPY",EDGE,{"derivedFrom":makeQuery(id+"F18.opExtrude","SWEPT_EDGE",EDGE,{"disambiguationData":[OSD([sQuery(id+"F17.wireOp",EDGE,"E65"),sQuery(id+"F17.wireOp",EDGE,"E67")])]})});
            var Q23;
            Q23=makeQuery(id+"F18.boolean.opBoolean","COPY",EDGE,{"derivedFrom":makeQuery(id+"F18.opExtrude","SWEPT_EDGE",EDGE,{"disambiguationData":[OSD([sQuery(id+"F17.wireOp",EDGE,"E61"),sQuery(id+"F17.wireOp",EDGE,"E62")])]})});
            fillet(context, id + "F19", {"entities" : qUnion([Q0, Q1, Q2, Q3, Q4, Q5, Q6, Q7, Q8, Q9, Q10, Q11, Q12, Q13, Q14, Q15, Q16, Q17, Q18, Q19, Q20, Q21, Q22, Q23]), "radius" : 2 * mm, "tangentPropagation" : true, "allowEdgeOverflow" : false});
        }
        {
            var Q0;
            Q0=makeQuery(id+"F10.boolean.opBoolean","MERGE",FACE,{"derivedFrom":[makeQuery(id+"F6.opExtrude","CAP_FACE",FACE,{"disambiguationData":[OSD([sQuery(id+"F5.wireOp",EDGE,"E20")])],"isStart":true}),makeQuery(id+"F10.opExtrude","SWEPT_FACE",FACE,{"disambiguationData":[OSD([sQuery(id+"F9.wireOp",EDGE,"E29")])]})]});
            var sketch = newSketch(context, id + "F20", { "sketchPlane" : qUnion([Q0])});
            skText(sketch, "E72", { "text": "PLUG + PLAY", "fontName": "OpenSans-Regular.ttf"});
            const initialGuessF20  = {"E72": [0.00746, 0.00511, 1, 0, 0.00653]};
            skSetInitialGuess(sketch, initialGuessF20);
            skSolve(sketch);
        }
        {
            var Q0;
            Q0 = qSketchRegion(id + "F20", true);
            extrude(context, id + "F21", {"entities" : qUnion([Q0]), "operationType" : NewBodyOperationType.REMOVE, "oppositeDirection" : true, "depth" : 25 * mm});
        }
        {
            var Q0;
            Q0=makeQuery(id+"F8.imprint","IMPRINT",FACE,{"disambiguationData":[TD([[makeQuery(id+"F8.imprint","IMPRINT",EDGE,{"derivedFrom":sQuery(id+"F8.wireOp",EDGE,"E22")}),1.0]])]});
            var Q1;
            Q1=sQuery(id+"F8.wireOp",EDGE,"E23");
            var Q2;
            Q2=sQuery(id+"F8.wireOp",EDGE,"E22");
            revolve(context, id + "F22", {"operationType" : NewBodyOperationType.ADD, "entities" : qUnion([Q0]), "surfaceEntities" : qUnion([Q1]), "axis" : qUnion([Q2]), "revolveType" : RevolveType.FULL});
        }
        {
            var Q0;
            {var subQ1=sQuery(id+"F9.wireOp",EDGE,"E25");Q0=makeQuery(id+"F13.boolean.opBoolean","SPLIT",FACE,{"disambiguationData":[TD([makeQuery(id+"F13.opExtrude","SWEPT_FACE",FACE,{"disambiguationData":[OSD([sQuery(id+"F12.wireOp",EDGE,"E34.sketch_text.stroke-0")])]})])],"derivedFrom":makeQuery(id+"F10.boolean.opBoolean","MERGE",FACE,{"derivedFrom":[makeQuery(id+"F6.opExtrude","CAP_FACE",FACE,{"disambiguationData":[OSD([sQuery(id+"F5.wireOp",EDGE,"E20")])],"isStart":false}),makeQuery(id+"F10.opExtrude","SWEPT_FACE",FACE,{"disambiguationData":[OSD([subQ1])]})]})});}
            cPlane(context, id + "F23", {"entities" : qUnion([Q0]), "cplaneType" : CPlaneType.OFFSET, "offset" : 5 * mm, "oppositeDirection" : true, "width" : 150 * mm, "height" : 150 * mm});
        }
        {
            var Q0;
            Q0=qCreatedBy(id+"F23.planeOp",FACE);
            var sketch = newSketch(context, id + "F24", { "sketchPlane" : qUnion([Q0])});
            skLineSegment(sketch, "E73.bottom", {"start": v(-51, 18.05) * mm, "end": v(-42.89, 18.05) * mm});
            skLineSegment(sketch, "E73.top", {"start": v(-51, 17.68) * mm, "end": v(-42.89, 17.68) * mm});
            skLineSegment(sketch, "E73.left", {"start": v(-51, 18.05) * mm, "end": v(-51, 17.68) * mm});
            skLineSegment(sketch, "E73.right", {"start": v(-42.89, 18.05) * mm, "end": v(-42.89, 17.68) * mm});
            skLineSegment(sketch, "E74.bottom", {"start": v(-29.8, 19.6) * mm, "end": v(-21.69, 19.6) * mm});
            skLineSegment(sketch, "E74.top", {"start": v(-29.8, 19.24) * mm, "end": v(-21.69, 19.24) * mm});
            skLineSegment(sketch, "E74.left", {"start": v(-29.8, 19.6) * mm, "end": v(-29.8, 19.24) * mm});
            skLineSegment(sketch, "E74.right", {"start": v(-21.69, 19.6) * mm, "end": v(-21.69, 19.24) * mm});
            skLineSegment(sketch, "E75.bottom", {"start": v(-17.86, 18.85) * mm, "end": v(-9.76, 18.85) * mm});
            skLineSegment(sketch, "E75.top", {"start": v(-17.86, 18.49) * mm, "end": v(-9.76, 18.49) * mm});
            skLineSegment(sketch, "E75.left", {"start": v(-17.86, 18.85) * mm, "end": v(-17.86, 18.49) * mm});
            skLineSegment(sketch, "E75.right", {"start": v(-9.76, 18.85) * mm, "end": v(-9.76, 18.49) * mm});
            skLineSegment(sketch, "E76.bottom", {"start": v(18.43, 17.76) * mm, "end": v(26.53, 17.76) * mm});
            skLineSegment(sketch, "E76.top", {"start": v(18.43, 17.4) * mm, "end": v(26.53, 17.4) * mm});
            skLineSegment(sketch, "E76.left", {"start": v(18.43, 17.76) * mm, "end": v(18.43, 17.4) * mm});
            skLineSegment(sketch, "E76.right", {"start": v(26.53, 17.76) * mm, "end": v(26.53, 17.4) * mm});
            skLineSegment(sketch, "E77.bottom", {"start": v(46.91, 19) * mm, "end": v(55.02, 19) * mm});
            skLineSegment(sketch, "E77.top", {"start": v(46.91, 18.64) * mm, "end": v(55.02, 18.64) * mm});
            skLineSegment(sketch, "E77.left", {"start": v(46.91, 19) * mm, "end": v(46.91, 18.64) * mm});
            skLineSegment(sketch, "E77.right", {"start": v(55.02, 19) * mm, "end": v(55.02, 18.64) * mm});
            skLineSegment(sketch, "E78.bottom", {"start": v(55.52, 19) * mm, "end": v(63.62, 19) * mm});
            skLineSegment(sketch, "E78.top", {"start": v(55.52, 18.64) * mm, "end": v(63.62, 18.64) * mm});
            skLineSegment(sketch, "E78.left", {"start": v(55.52, 19) * mm, "end": v(55.52, 18.64) * mm});
            skLineSegment(sketch, "E78.right", {"start": v(63.62, 19) * mm, "end": v(63.62, 18.64) * mm});
            skLineSegment(sketch, "E79.bottom", {"start": v(26.5, 19.25) * mm, "end": v(34.6, 19.25) * mm});
            skLineSegment(sketch, "E79.top", {"start": v(26.5, 18.89) * mm, "end": v(34.6, 18.89) * mm});
            skLineSegment(sketch, "E79.left", {"start": v(26.5, 19.25) * mm, "end": v(26.5, 18.89) * mm});
            skLineSegment(sketch, "E79.right", {"start": v(34.6, 19.25) * mm, "end": v(34.6, 18.89) * mm});
            skLineSegment(sketch, "E80.bottom", {"start": v(9.9, 18.27) * mm, "end": v(18, 18.27) * mm});
            skLineSegment(sketch, "E80.top", {"start": v(9.9, 17.9) * mm, "end": v(18, 17.9) * mm});
            skLineSegment(sketch, "E80.left", {"start": v(9.9, 18.27) * mm, "end": v(9.9, 17.9) * mm});
            skLineSegment(sketch, "E80.right", {"start": v(18, 18.27) * mm, "end": v(18, 17.9) * mm});
            skLineSegment(sketch, "E81.bottom", {"start": v(10.2, 22.86) * mm, "end": v(18.3, 22.86) * mm});
            skLineSegment(sketch, "E81.top", {"start": v(10.2, 22.5) * mm, "end": v(18.3, 22.5) * mm});
            skLineSegment(sketch, "E81.left", {"start": v(10.2, 22.86) * mm, "end": v(10.2, 22.5) * mm});
            skLineSegment(sketch, "E81.right", {"start": v(18.3, 22.86) * mm, "end": v(18.3, 22.5) * mm});
            skLineSegment(sketch, "E82.bottom", {"start": v(-62.99, 5.84) * mm, "end": v(-57.87, 5.84) * mm});
            skLineSegment(sketch, "E82.top", {"start": v(-62.99, 5.42) * mm, "end": v(-57.87, 5.42) * mm});
            skLineSegment(sketch, "E82.left", {"start": v(-62.99, 5.84) * mm, "end": v(-62.99, 5.42) * mm});
            skLineSegment(sketch, "E82.right", {"start": v(-57.87, 5.84) * mm, "end": v(-57.87, 5.42) * mm});
            skLineSegment(sketch, "E83.bottom", {"start": v(-58.13, 5.13) * mm, "end": v(-53.02, 5.13) * mm});
            skLineSegment(sketch, "E83.top", {"start": v(-58.13, 4.7) * mm, "end": v(-53.02, 4.7) * mm});
            skLineSegment(sketch, "E83.left", {"start": v(-58.13, 5.13) * mm, "end": v(-58.13, 4.7) * mm});
            skLineSegment(sketch, "E83.right", {"start": v(-53.02, 5.13) * mm, "end": v(-53.02, 4.7) * mm});
            skLineSegment(sketch, "E84.bottom", {"start": v(-58.45, 7.86) * mm, "end": v(-53.34, 7.86) * mm});
            skLineSegment(sketch, "E84.top", {"start": v(-58.45, 7.44) * mm, "end": v(-53.34, 7.44) * mm});
            skLineSegment(sketch, "E84.left", {"start": v(-58.45, 7.86) * mm, "end": v(-58.45, 7.44) * mm});
            skLineSegment(sketch, "E84.right", {"start": v(-53.34, 7.86) * mm, "end": v(-53.34, 7.44) * mm});
            skLineSegment(sketch, "E85.bottom", {"start": v(-53.91, 6.58) * mm, "end": v(-48.8, 6.58) * mm});
            skLineSegment(sketch, "E85.top", {"start": v(-53.91, 6.16) * mm, "end": v(-48.8, 6.16) * mm});
            skLineSegment(sketch, "E85.left", {"start": v(-53.91, 6.58) * mm, "end": v(-53.91, 6.16) * mm});
            skLineSegment(sketch, "E85.right", {"start": v(-48.8, 6.58) * mm, "end": v(-48.8, 6.16) * mm});
            skLineSegment(sketch, "E86.bottom", {"start": v(-67.86, 7.52) * mm, "end": v(-62.75, 7.52) * mm});
            skLineSegment(sketch, "E86.top", {"start": v(-67.86, 7.1) * mm, "end": v(-62.75, 7.1) * mm});
            skLineSegment(sketch, "E86.left", {"start": v(-67.86, 7.52) * mm, "end": v(-67.86, 7.1) * mm});
            skLineSegment(sketch, "E86.right", {"start": v(-62.75, 7.52) * mm, "end": v(-62.75, 7.1) * mm});
            skLineSegment(sketch, "E87.bottom", {"start": v(-43.36, 6.3) * mm, "end": v(-38.25, 6.3) * mm});
            skLineSegment(sketch, "E87.top", {"start": v(-43.36, 5.87) * mm, "end": v(-38.25, 5.87) * mm});
            skLineSegment(sketch, "E87.left", {"start": v(-43.36, 6.3) * mm, "end": v(-43.36, 5.87) * mm});
            skLineSegment(sketch, "E87.right", {"start": v(-38.25, 6.3) * mm, "end": v(-38.25, 5.87) * mm});
            skLineSegment(sketch, "E88.bottom", {"start": v(-33.15, 6.13) * mm, "end": v(-28.04, 6.13) * mm});
            skLineSegment(sketch, "E88.top", {"start": v(-33.15, 5.7) * mm, "end": v(-28.04, 5.7) * mm});
            skLineSegment(sketch, "E88.left", {"start": v(-33.15, 6.13) * mm, "end": v(-33.15, 5.7) * mm});
            skLineSegment(sketch, "E88.right", {"start": v(-28.04, 6.13) * mm, "end": v(-28.04, 5.7) * mm});
            skSolve(sketch);
        }
        {
            var Q0;
            Q0 = qSketchRegion(id + "F24", true);
            extrude(context, id + "F25", {"entities" : qUnion([Q0]), "operationType" : NewBodyOperationType.ADD, "endBound" : BoundingType.SYMMETRIC, "depth" : 2 * mm});
        }
        {
            var Q0;
            {var subQ0=sQuery(id+"F9.wireOp",EDGE,"E29");var subQ3=sQuery(id+"F14.wireOp",EDGE,"E36");Q0=makeQuery(id+"F21.boolean.opBoolean","SPLIT",FACE,{"disambiguationData":[TD([makeQuery(id+"F15.boolean.opBoolean","COPY",FACE,{"derivedFrom":makeQuery(id+"F15.opExtrude","SWEPT_FACE",FACE,{"disambiguationData":[OSD([subQ3])]})})])],"derivedFrom":makeQuery(id+"F10.boolean.opBoolean","MERGE",FACE,{"derivedFrom":[makeQuery(id+"F6.opExtrude","CAP_FACE",FACE,{"disambiguationData":[OSD([sQuery(id+"F5.wireOp",EDGE,"E20")])],"isStart":true}),makeQuery(id+"F10.opExtrude","SWEPT_FACE",FACE,{"disambiguationData":[OSD([subQ0])]})]})});}
            cPlane(context, id + "F26", {"entities" : qUnion([Q0]), "cplaneType" : CPlaneType.OFFSET, "offset" : 5 * mm, "oppositeDirection" : true, "width" : 150 * mm, "height" : 150 * mm});
        }
        {
            var Q0;
            Q0=qCreatedBy(id+"F26.planeOp",FACE);
            var sketch = newSketch(context, id + "F27", { "sketchPlane" : qUnion([Q0])});
            skLineSegment(sketch, "E89.bottom", {"start": v(6.92, 9.94) * mm, "end": v(13.12, 9.94) * mm});
            skLineSegment(sketch, "E89.top", {"start": v(6.92, 9.23) * mm, "end": v(13.12, 9.23) * mm});
            skLineSegment(sketch, "E89.left", {"start": v(6.92, 9.94) * mm, "end": v(6.92, 9.23) * mm});
            skLineSegment(sketch, "E89.right", {"start": v(13.12, 9.94) * mm, "end": v(13.12, 9.23) * mm});
            skLineSegment(sketch, "E90.bottom", {"start": v(41, 9.83) * mm, "end": v(46.31, 9.83) * mm});
            skLineSegment(sketch, "E90.top", {"start": v(41, 9.23) * mm, "end": v(46.31, 9.23) * mm});
            skLineSegment(sketch, "E90.left", {"start": v(41, 9.83) * mm, "end": v(41, 9.23) * mm});
            skLineSegment(sketch, "E90.right", {"start": v(46.31, 9.83) * mm, "end": v(46.31, 9.23) * mm});
            skLineSegment(sketch, "E91.bottom", {"start": v(51.55, 9.83) * mm, "end": v(55.96, 9.83) * mm});
            skLineSegment(sketch, "E91.top", {"start": v(51.55, 9.23) * mm, "end": v(55.96, 9.23) * mm});
            skLineSegment(sketch, "E91.left", {"start": v(51.55, 9.83) * mm, "end": v(51.55, 9.23) * mm});
            skLineSegment(sketch, "E91.right", {"start": v(55.96, 9.83) * mm, "end": v(55.96, 9.23) * mm});
            skSolve(sketch);
        }
        {
            var Q0;
            Q0 = qSketchRegion(id + "F27", true);
            extrude(context, id + "F28", {"entities" : qUnion([Q0]), "operationType" : NewBodyOperationType.ADD, "endBound" : BoundingType.SYMMETRIC, "depth" : 2 * mm});
        }
        {
            var Q0;
            Q0=makeQuery(id+"F10.opExtrude","SWEPT_FACE",FACE,{"disambiguationData":[OSD([sQuery(id+"F9.wireOp",EDGE,"E24.top")])]});
            var sketch = newSketch(context, id + "F29", { "sketchPlane" : qUnion([Q0])});
            skCircle(sketch, "E92.cCircle", {"center": v(0, 0) * mm, "radius": 56.76 * mm, "construction": true});
            skLineSegment(sketch, "E92.0", {"start": v(32.77, -56.76) * mm, "end": v(-32.77, -56.76) * mm});
            skLineSegment(sketch, "E92.1", {"start": v(-32.77, -56.76) * mm, "end": v(-65.54, 0) * mm});
            skLineSegment(sketch, "E92.2", {"start": v(-65.54, 0) * mm, "end": v(-32.77, 56.76) * mm});
            skLineSegment(sketch, "E92.3", {"start": v(-32.77, 56.76) * mm, "end": v(32.77, 56.76) * mm});
            skLineSegment(sketch, "E92.4", {"start": v(32.77, 56.76) * mm, "end": v(65.54, 0) * mm});
            skLineSegment(sketch, "E92.5", {"start": v(65.54, 0) * mm, "end": v(32.77, -56.76) * mm});
            skPoint(sketch, "E92.0.midPoint", {"position": v(0, -56.76) * mm});
            skSolve(sketch);
        }
        {
            var Q0;
            Q0 = qSketchRegion(id + "F29", true);
            extrude(context, id + "F30", {"entities" : qUnion([Q0]), "operationType" : NewBodyOperationType.ADD, "depth" : 15 * mm, "offsetDistance" : 25 * mm});
        }
        {
            var Q0;
            Q0=makeQuery(id+"F30.opExtrude","SWEPT_EDGE",EDGE,{"disambiguationData":[OSD([sQuery(id+"F29.wireOp",EDGE,"E92.0"),sQuery(id+"F29.wireOp",EDGE,"E92.1")])]});
            var Q1;
            Q1=makeQuery(id+"F30.opExtrude","SWEPT_EDGE",EDGE,{"disambiguationData":[OSD([sQuery(id+"F29.wireOp",EDGE,"E92.1"),sQuery(id+"F29.wireOp",EDGE,"E92.2")])]});
            var Q2;
            Q2=makeQuery(id+"F30.opExtrude","SWEPT_EDGE",EDGE,{"disambiguationData":[OSD([sQuery(id+"F29.wireOp",EDGE,"E92.2"),sQuery(id+"F29.wireOp",EDGE,"E92.3")])]});
            var Q3;
            Q3=makeQuery(id+"F30.opExtrude","SWEPT_EDGE",EDGE,{"disambiguationData":[OSD([sQuery(id+"F29.wireOp",EDGE,"E92.3"),sQuery(id+"F29.wireOp",EDGE,"E92.4")])]});
            var Q4;
            Q4=makeQuery(id+"F30.opExtrude","SWEPT_EDGE",EDGE,{"disambiguationData":[OSD([sQuery(id+"F29.wireOp",EDGE,"E92.4"),sQuery(id+"F29.wireOp",EDGE,"E92.5")])]});
            var Q5;
            Q5=makeQuery(id+"F30.opExtrude","SWEPT_EDGE",EDGE,{"disambiguationData":[OSD([sQuery(id+"F29.wireOp",EDGE,"E92.0"),sQuery(id+"F29.wireOp",EDGE,"E92.5")])]});
            fillet(context, id + "F31", {"entities" : qUnion([Q0, Q1, Q2, Q3, Q4, Q5]), "radius" : 5 * mm, "tangentPropagation" : true, "allowEdgeOverflow" : false});
        }
    });
